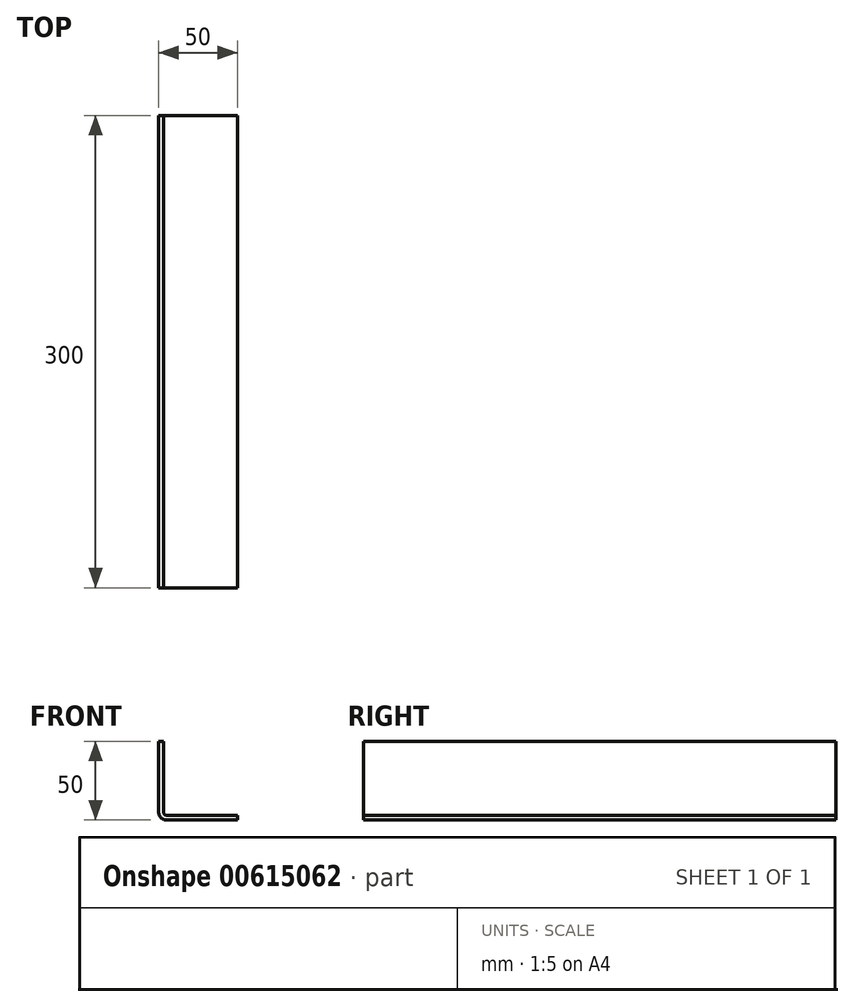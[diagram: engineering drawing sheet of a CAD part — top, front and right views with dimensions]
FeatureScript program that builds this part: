
annotation { "Feature Type Name" : "Feature", "Feature Type Description" : "" }
export const myFeature = defineFeature(function(context is Context, id is Id, definition is map)
    precondition{}
    {
        {
            var Q0;
            Q0=qCreatedBy(makeId("Front.planeOp"),FACE);
            var sketch = newSketch(context, id + "F0", { "sketchPlane" : qUnion([Q0])});
            skLineSegment(sketch, "E0.bottom", {"start": v(0, 0) * mm, "end": v(3, 0) * mm});
            skLineSegment(sketch, "E0.top", {"start": v(0, 50) * mm, "end": v(3, 50) * mm});
            skLineSegment(sketch, "E0.left", {"start": v(0, 5) * mm, "end": v(0, 50) * mm});
            skLineSegment(sketch, "E0.right", {"start": v(3, 5) * mm, "end": v(3, 50) * mm});
            skLineSegment(sketch, "E1.bottom", {"start": v(5, 0) * mm, "end": v(50, 0) * mm});
            skLineSegment(sketch, "E1.top", {"start": v(5, 3) * mm, "end": v(50, 3) * mm});
            skLineSegment(sketch, "E1.right", {"start": v(50, 0) * mm, "end": v(50, 3) * mm});
            skArc(sketch, "E2.filletArc", {"start": v(3, 5) * mm, "mid": v(3.59, 3.59) * mm, "end": v(5, 3) * mm});
            skPoint(sketch, "E3.visualSharp", {"position": v(0, 0) * mm});
            skArc(sketch, "E3.filletArc", {"start": v(0, 5) * mm, "mid": v(1.46, 1.46) * mm, "end": v(5, 0) * mm});
            skSolve(sketch);
        }
        {
            var Q0;
            Q0 = qSketchRegion(id + "F0", true);
            extrude(context, id + "F1", {"entities" : qUnion([Q0]), "depth" : 300 * mm, "offsetDistance" : 25 * mm});
        }
    });
